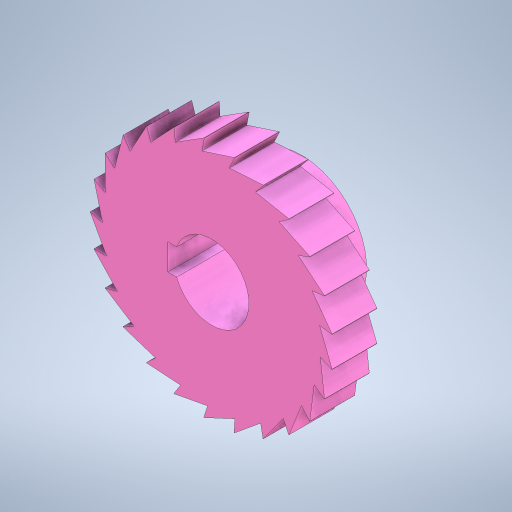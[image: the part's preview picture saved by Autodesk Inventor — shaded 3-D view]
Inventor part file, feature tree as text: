
AUTODESK INVENTOR PART (.ipt)
format: ipt  version: 2024 (Build 280153000, 153)  size: 389,632 bytes
history: native  units: mm
features: sketch x5, extrude x4, other x1, pattern_circular x1
ambient origin geometry x8: Origin, YZ Plane, XZ Plane, XY Plane, X Axis, Y Axis, Z Axis, Center Point
bodies: Body1 (feature_tree)
feature tree (11):
  other  "Sólido1"
  extrude  "Extrusión1"  Depth=20.0mm
  extrude  "Extrusión2"  TaperAngle=15.0deg  [1 undecoded]
  pattern_circular  "Patrón circular1"  Count=25 Angle=360.0deg
  extrude  "Extrusión3"  Depth=24.0mm
  sketch  "Boceto4"  dims[d7=8.0mm]
  extrude  "Extrusión4"  Depth=12.0mm TaperAngle=0.0deg
  sketch  "Boceto1"  dims[d0=65.0mm d1=20.0mm]
  sketch  "Boceto2"  dims[d2=12.0mm d3=0.0mm d4=15.0deg]
  sketch  "Boceto3"  dims[d5=8.0mm]
  sketch  "Boceto5"  dims[d8=12.0mm d9=0.0mm d10=250.0mm d11=360.0deg d13=35.0mm d14=12.0mm d15=0.0mm d22=20.0mm d23=20.0mm d24=3.45mm d25=7.0mm d26=24.0mm d27=0.0mm]
note: 1 required parameter value undecoded (feature->parameter linkage not recoverable at this tier; creation-order binding heuristic only, values carry confidence <= 0.55)
